# Revit family: Kimberley Clark Professional MR2 Bath Tissue Dispenser SS 426130 Family
name_source: partatom
category: Generic Models
revit_build: Autodesk Revit 2018 (Build: 20170223_1515(x64)
units: mm (PartAtom-declared; Revit-internal decimal feet)

## family parameters
Always vertical = Yes
Can host rebar = No
Cut with Voids When Loaded = No
Host = Wall
Part Type = Normal
Room Calculation Point = No
Round Connector Dimension = Use Diameter
Shared = No

## types (1)
- Kimberley Clark Professional MR2 Bath Tissue Dispenser SS
    Distance From Floor = 1000 mm  [stored 3.28084 ft]
    Height = 265 mm
    Material = Rubber - Black
    Material 2 = Stainless - Polished
    Model = Kimberley Clark Professional MR2 Bath Tissue Dispenser SS
    Telephone = 011 456 5911
    URL = www.kcprofessional.com
    Width = 136 mm

note: [stored X ft] marks values corroborated as IEEE doubles in the binary element streams (Revit-internal decimal feet)

## geometry (parser evidence)
native form markers: Sweep x2
no freeform markers — native parametric forms only
